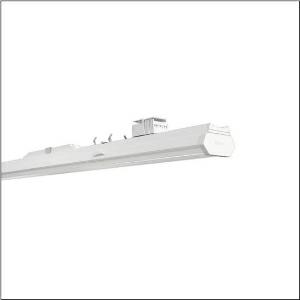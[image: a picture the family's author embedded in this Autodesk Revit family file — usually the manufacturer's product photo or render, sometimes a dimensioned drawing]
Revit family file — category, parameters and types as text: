
# Revit family: licross_11_protected_mo_51td117n485g
name_source: partatom
category: Lighting Fixtures
units: mm (PartAtom-declared; Revit-internal decimal feet)

## family parameters
Cut with Voids When Loaded = No
Host = Face
Light Source = No
Part Type = Normal
Room Calculation Point = No
Round Connector Dimension = Use Diameter
Shared = No

## types (1)
- Licross 11 Protected MO (1 x LED, 8680 lm, 48.6 W, 4000K)
    Apparent Load = 49 VA
    CIE Flux Codes = 83 94 98 100 100
    Color Rendering = 80
    Color Temperature = 4000K
    Default Elevation = 1800 mm
    Description = Licross 11 Protected MO, luminaire insert, of sheet steel, galvanised, coil coated, white, length: 1.500mm, width: 90mm, height: 101mm, LED rated luminous flux: 8.680lm, light colour: 840, SDCM (Standard Deviation of Colour Matching)MacAdam ≤ 2 SDCM (initial), control gear: ON/OFF, with plug, 3-pole, with phase selection, mains connection: 220..240V, AC, 50/60Hz, rated input power: 49W, internal wiring halogen-free, primary light control with lens, of plastic, primary optical cover: cover, of PMMA, light emission: direct distribution, primary light characteristic: symmetric, protection rating (complete): IP54, insulation class (complete): insulation class I (protective earthing), certification: CE, ENEC, VDE, UKCA, protection symbol: D if used in an environment with non-conductive dust loads with corresponding accessories, impact resistance: IK06, permissible ambient temperature for indoor applications: -25..+35°C, corresponds to IFS (International Featured Standards) requirements for safety and quality in the food industry, reducing of maximum allowable ambient temperature of 5°C with ceiling mounting, LABS conformity tested according to VDMA 24364:2018-05, The light source and the operating device comply with the requirements of the Ecodesign Regulation (EU) 2019/2020 and are replaceable in accordance with this regulation, packaging unit: 1 piece
    Height = 92 mm
    Lamp = 1 x LED
    Lamp Light Flux = 8680 lm
    Lamp Power = 48.6 W
    Lamp count = 1
    Length = 1500 mm
    Luminous efficacy = 179 lm/W
    Manufacturer = Siteco
    ModVariant = No
    Model = 51TD117N485G
    Mounting Place = Ceiling
    Mounting Type = Pendant
    Number of Poles = 1
    OnlyDefault = Yes
    Power Factor = 1
    Product Name = Licross 11 Protected MO
    Product group = luminaire insert | ceiling pendant
    ProductGroupID = 901
    Protection Class = Protection class I
    Protection Degree = IP 54
    RLX_Detail_Level = 1
    RLX_Emergency_Light_Flux = 0 lm
    RLX_Emergency_Type = 0
    RLX_Emergency_Type_DB = No
    RlxData = <blob elided: 20745 chars, md5=d8739a44>
    Socket = socket
    Standby Power = 0 W
    System Light Flux = 8680 lm
    System Power = 49 W
    Type Comments = Product without accessories
    Type Image = l_1256145.jpg
    URL = http://relux.com
    VarID = ---
    Voltage = 0 V
    Weight = 0.00 kg
    Width = 88 mm

## geometry (parser evidence)
native form markers: Blend x4, Sweep x12
no freeform markers — native parametric forms only
